SOLIDWORKS PART (.sldprt)
format: sldprt  version: not decoded by parser v0  size: 135,680 bytes
history: native  units: mm
features: sketch x4, extrude x3, material x1, cut_extrude x1, fillet x1, chamfer x1 (+13 scaffold rows collapsed)
feature tree (24):
  scaffold x13  (default folders/planes/origin — collapsed)
  material  "Material <not specified>"
  sketch  "Sketch1"  dims[D1=3.5mm D2=3.5mm D3=7.0mm]
  extrude  "Boss-Extrude1"  Depth=2.3mm
  sketch  "Sketch3"
  extrude  "Boss-Extrude2"  Depth=2mm
  sketch  "Sketch4"  dims[c1.D1=~1.498296mm c1.D2=7.0mm c2.D1=3.0mm]
  extrude  "Boss-Extrude3"  Depth=7mm
  sketch  "Sketch5"  dims[D1=3.1mm D2=3.5mm]
  cut_extrude  "Cut-Extrude1"  [1 undecoded]
  fillet  "Fillet1"  Radius=2mm
  chamfer  "Chamfer1"  Distance=1mm Angle=45deg
decode coverage: 8 of 10 modeling features carry decoded parameters
note: ~ marks probable driven/reference dimensions
note: 1 parameter value undecoded
note: suppression state not decoded; provenance and decode notes live in map.json
